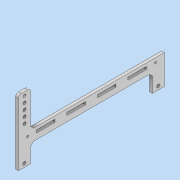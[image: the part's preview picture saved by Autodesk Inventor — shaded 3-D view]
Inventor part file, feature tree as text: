
AUTODESK INVENTOR PART (.ipt)
format: ipt  version: 2022 (Build 260153000, 153)  size: 323,584 bytes
history: native  units: mm
features: sketch x9, extrude x6, other x6, hole x3, chamfer x2, fillet x2, reference x2, projected_geometry x1
ambient origin geometry x8: Origin, YZ Plane, XZ Plane, XY Plane, X Axis, Y Axis, Z Axis, Center Point
bodies: Solid1 (feature_tree)
feature tree (31):
  extrude  "Extrusion1"  Depth=38.1mm
  sketch  "Sketch2"  dims[d4=38.1mm d5=24.0mm]
  extrude  "Extrusion3"  Depth=24.0mm
  chamfer  "Chamfer1"  Distance=6.0mm
  chamfer  "Chamfer2"  Distance=39.0017mm
  fillet  "Fillet1"  Radius=25.4mm
  sketch  "Sketch4"  dims[d16=308.4068mm]
  sketch  "Sketch5"  dims[d17=6.0mm]
  hole  "Hole1"  [1 undecoded]
  hole  "Hole2"  [1 undecoded]
  hole  "Hole3"  [1 undecoded]
  extrude  "Extrusion6"  TaperAngle=0.0deg  [1 undecoded]
  extrude  "Extrusion7"  Depth=6.35mm TaperAngle=45.0deg
  fillet  "Fillet2"  Radius=6.35mm
  extrude  "Extrusion8"  Depth=6.35mm
  extrude  "Extrusion9"  Depth=25.4mm
  sketch  "Sketch1"  dims[d1=38.1mm d2=38.1mm]
  reference  "Reference1"
  reference  "Reference2"
  sketch  "Sketch3"  dims[d6=76.2mm]
  sketch  "Sketch6"  dims[d18=39.0017mm]
  sketch  "Sketch7"  dims[d21=6.0mm]
  sketch  "Sketch8"  dims[d22=39.0017mm]
  sketch  "Sketch9"  dims[d23=25.4mm d24=6.0mm d25=39.0017mm d26=25.4mm d27=6.0mm d28=39.0017mm d29=25.4mm d33=6.0mm d34=0.0mm d37=12.7mm d38=0.0mm d39=0.0mm d40=6.35mm d41=3.175mm d42=45.0deg d43=6.35mm d44=3.175mm d45=45.0deg d46=6.35mm d49=25.4mm d50=6.35mm d51=7.62mm d52=50.0mm d54=12.7mm d55=10.0mm d57=25.4mm d61=38.1mm d62=50.099999mm d63=3.2512mm d64=3.2512mm d65=19.05mm d66=19.05mm d69=6.604mm d70=19.05mm d71=14.5542mm d72=4.3688mm d73=90.0deg d74=17.0942mm d75=20.594885mm d76=6.604mm d77=19.05mm d78=14.5542mm d79=4.3688mm d80=90.0deg d81=17.0942mm d82=20.594885mm d83=4.4958mm d84=19.05mm d85=8.001mm d86=3.9878mm d87=90.0deg d88=17.0942mm d89=20.594885mm d90=38.1mm d91=0.125mm d92=0.125mm d93=0.0mm d94=0.0mm d95=6.37mm d96=6.37mm d97=0.0mm d98=0.0mm d99=6.35mm d100=4.246mm d101=4.246mm d102=6.354mm d103=6.354mm d104=6.354mm d105=6.354mm d106=6.354mm d107=6.354mm d108=6.354mm d109=10.0mm d110=0.0mm d111=5.55mm d112=0.0mm d113=0.0mm d114=0.0mm d115=0.0mm d116=0.0mm d117=0.0mm d118=0.0mm d119=0.0mm d120=6.0mm d121=0.0mm]
  projected_geometry  "Projected Loop1"
  other  "<userpath>\Desktop\P3 Bracket Files\V3 Baseplate.iam"
  other  "V3 Baseplate.iam"
  other  "QBot:1"
  other  "A002-596_A002-596-01_32"
  other  "C005-958_01_74"
  other  "C005-958_01_101"
note: 4 required parameter values undecoded (feature->parameter linkage not recoverable at this tier; creation-order binding heuristic only, values carry confidence <= 0.55)
